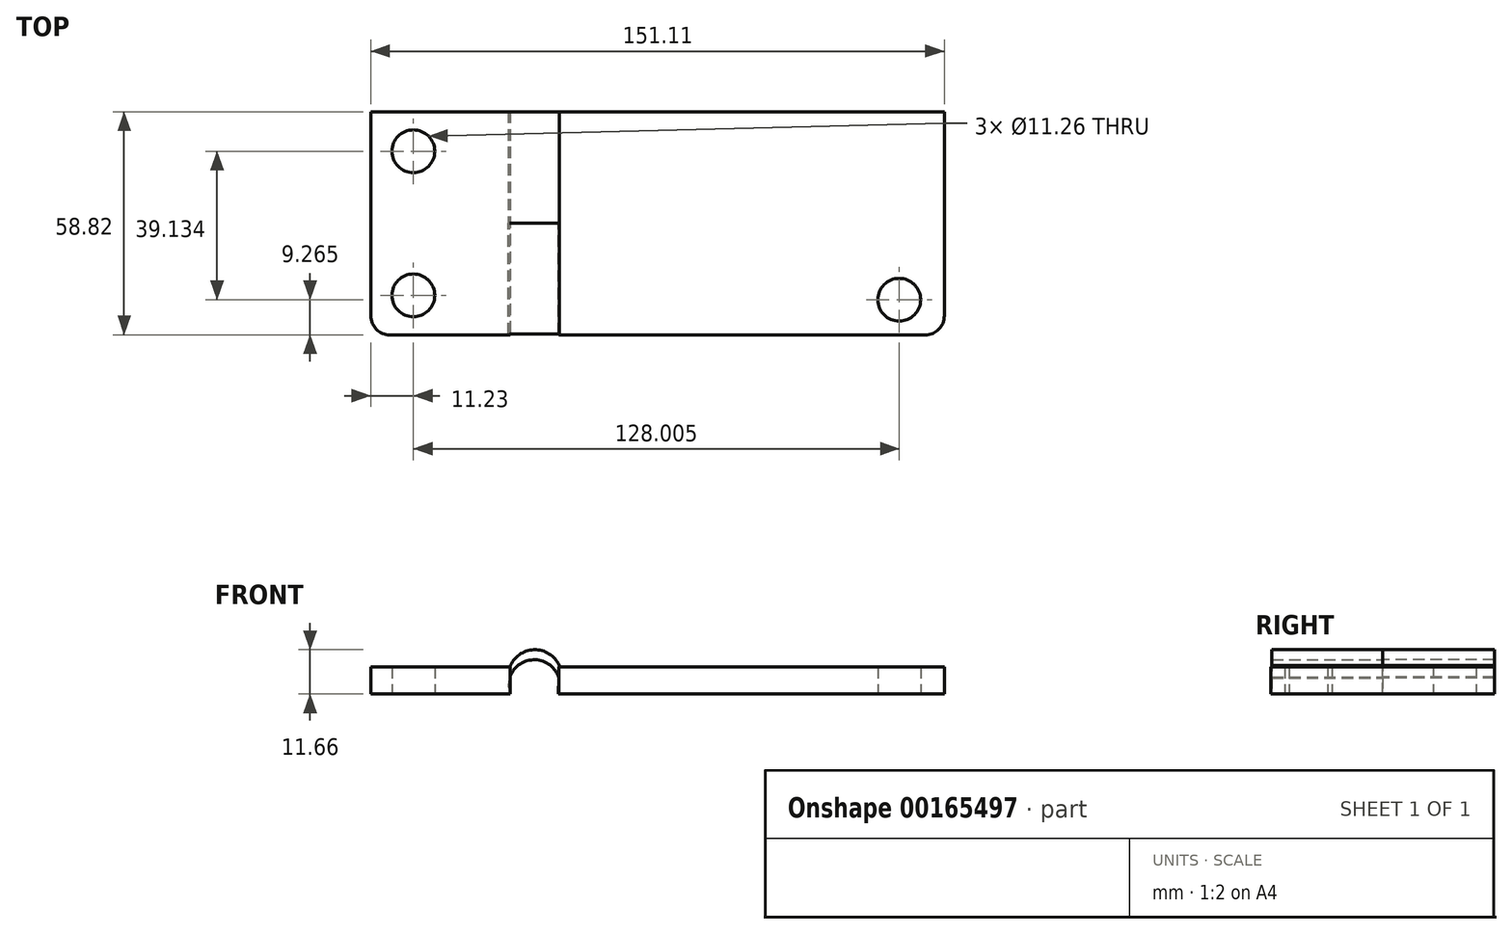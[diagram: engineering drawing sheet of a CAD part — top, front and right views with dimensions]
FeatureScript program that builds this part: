
annotation { "Feature Type Name" : "Feature", "Feature Type Description" : "" }
export const myFeature = defineFeature(function(context is Context, id is Id, definition is map)
    precondition{}
    {
        {
            var Q0;
            Q0=qCreatedBy(makeId("Top.planeOp"),FACE);
            var sketch = newSketch(context, id + "F0", { "sketchPlane" : qUnion([Q0])});
            skLineSegment(sketch, "E0.bottom", {"start": v(-43.9, 29.41) * mm, "end": v(107.2, 29.41) * mm});
            skLineSegment(sketch, "E0.top", {"start": v(-43.9, -29.41) * mm, "end": v(107.2, -29.41) * mm});
            skLineSegment(sketch, "E0.left", {"start": v(-43.9, 29.41) * mm, "end": v(-43.9, -29.41) * mm});
            skLineSegment(sketch, "E0.right", {"start": v(107.2, 29.41) * mm, "end": v(107.2, -29.41) * mm});
            skLineSegment(sketch, "E1.bottom", {"start": v(-7.17, 38.37) * mm, "end": v(5.67, 38.37) * mm});
            skLineSegment(sketch, "E1.top", {"start": v(-7.17, -40.76) * mm, "end": v(5.67, -40.76) * mm});
            skLineSegment(sketch, "E1.left", {"start": v(-7.17, 38.37) * mm, "end": v(-7.17, -40.76) * mm});
            skLineSegment(sketch, "E1.right", {"start": v(5.67, 38.37) * mm, "end": v(5.67, -40.76) * mm});
            skCircle(sketch, "E2", {"center": v(-32.67, 18.99) * mm, "radius": 5.63 * mm});
            skCircle(sketch, "E3.MirrorC", {"center": v(-32.67, -18.99) * mm, "radius": 5.63 * mm});
            skCircle(sketch, "E4.MirrorC", {"center": v(95.33, -20.15) * mm, "radius": 5.63 * mm});
            skSolve(sketch);
        }
        {
            var Q0;
            {var subQ0=sQuery(id+"F0.wireOp",EDGE,"E0.left");Q0=makeQuery(id+"F0.imprint","IMPRINT",FACE,{"disambiguationData":[TD([[makeQuery(id+"F0.imprint","IMPRINT",EDGE,{"derivedFrom":subQ0}),1.0]])]});}
            var Q1;
            {var subQ0=sQuery(id+"F0.wireOp",EDGE,"E0.right");Q1=makeQuery(id+"F0.imprint","IMPRINT",FACE,{"disambiguationData":[TD([[makeQuery(id+"F0.imprint","IMPRINT",EDGE,{"derivedFrom":subQ0}),-1.0]])]});}
            extrude(context, id + "F1", {"entities" : qUnion([Q0, Q1]), "depth" : 7.1 * mm});
        }
        {
            var Q0;
            Q0=qCreatedBy(makeId("Front.planeOp"),FACE);
            var sketch = newSketch(context, id + "F2", { "sketchPlane" : qUnion([Q0])});
            skArc(sketch, "E5", {"start": v(5.74, 7.54) * mm, "mid": v(-0.9, 11.66) * mm, "end": v(-7.25, 7.1) * mm});
            skArc(sketch, "E6", {"start": v(5.59, 0) * mm, "mid": v(-0.83, 9.02) * mm, "end": v(-7.25, 0) * mm});
            skLineSegment(sketch, "E7", {"start": v(-7.25, 0) * mm, "end": v(-7.25, 7.1) * mm});
            skLineSegment(sketch, "E8", {"start": v(5.59, 0) * mm, "end": v(5.74, 7.54) * mm});
            skSolve(sketch);
        }
        {
            var Q0;
            Q0 = qSketchRegion(id + "F2", true);
            extrude(context, id + "F3", {"entities" : qUnion([Q0]), "depth" : 29.2 * mm});
        }
        {
            var Q0;
            Q0 = qSketchRegion(id + "F2", true);
            extrude(context, id + "F4", {"entities" : qUnion([Q0]), "oppositeDirection" : true, "depth" : 29.4 * mm});
        }
        {
            var Q0;
            Q0=makeQuery(id+"F1.opExtrude","SWEPT_EDGE",EDGE,{"disambiguationData":[OSD([sQuery(id+"F0.wireOp",EDGE,"E0.top"),sQuery(id+"F0.wireOp",EDGE,"E0.left")])]});
            var Q1;
            Q1=makeQuery(id+"F1.opExtrude","SWEPT_EDGE",EDGE,{"disambiguationData":[OSD([sQuery(id+"F0.wireOp",EDGE,"E0.top"),sQuery(id+"F0.wireOp",EDGE,"E0.right")])]});
            fillet(context, id + "F5", {"entities" : qUnion([Q0, Q1]), "radius" : 5 * mm, "tangentPropagation" : true, "allowEdgeOverflow" : false});
        }
    });
